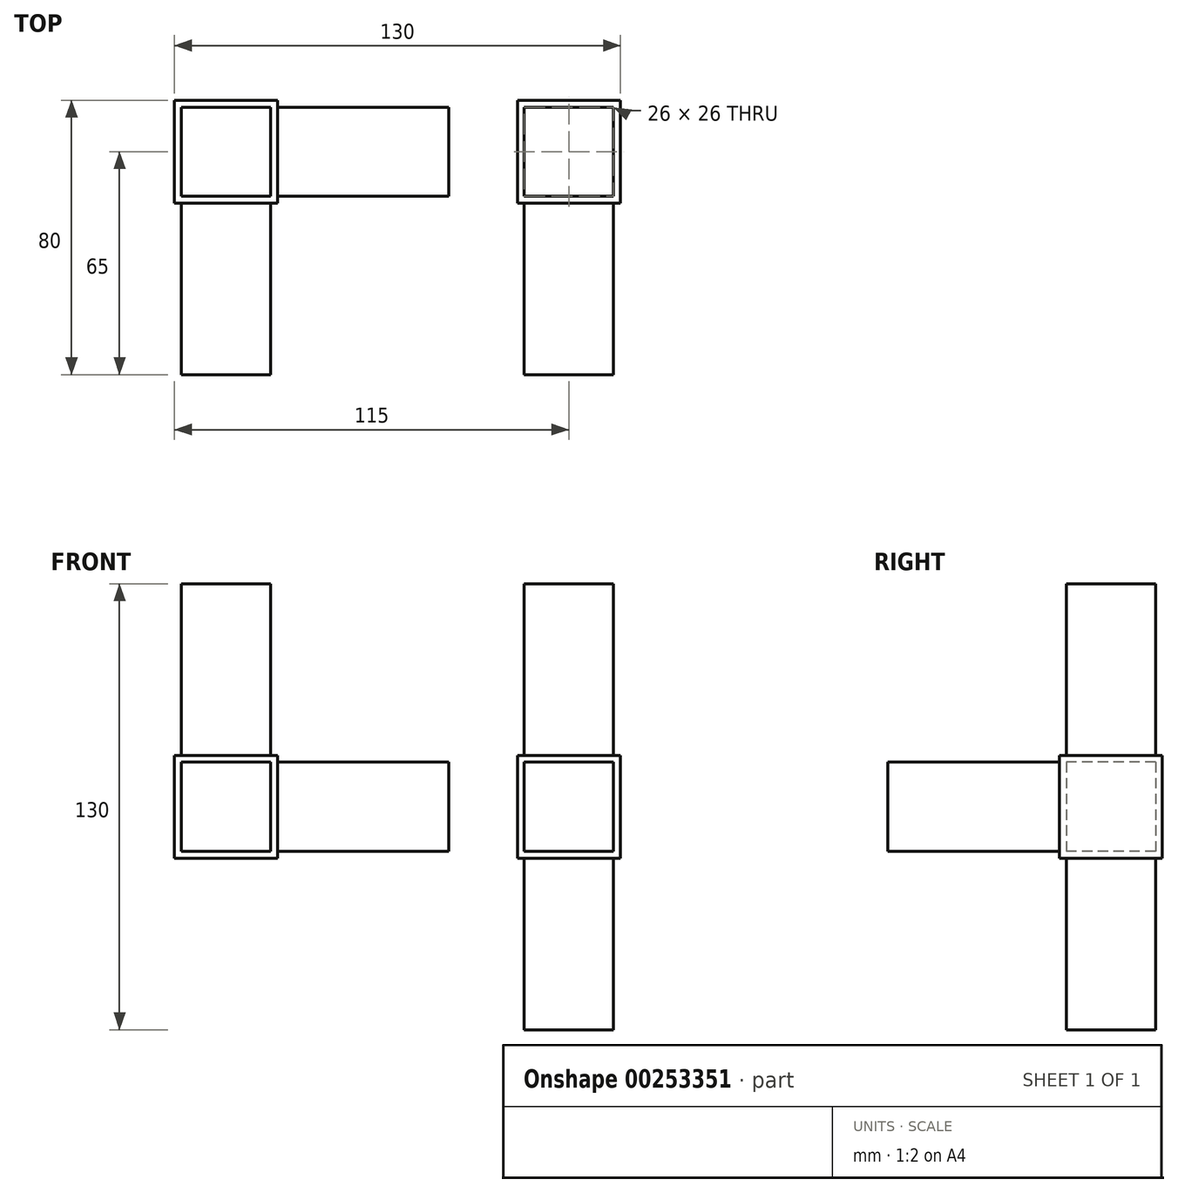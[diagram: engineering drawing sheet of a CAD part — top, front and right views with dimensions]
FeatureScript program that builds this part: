
annotation { "Feature Type Name" : "Feature", "Feature Type Description" : "" }
export const myFeature = defineFeature(function(context is Context, id is Id, definition is map)
    precondition{}
    {
        {
            assignVariable(context, id + "F0", {"name" : "Aussendurchmesser", "anyValue" : 30 * mm});
        }
        {
            assignVariable(context, id + "F1", {"name" : "Zapfenlaenge", "anyValue" : 50 * mm});
        }
        {
            var Q0;
            Q0=qCreatedBy(makeId("Top.planeOp"),FACE);
            var sketch = newSketch(context, id + "F2", { "sketchPlane" : qUnion([Q0])});
            skLineSegment(sketch, "E0.bottom", {"start": v(0, 0) * mm, "end": v(30, 0) * mm});
            skLineSegment(sketch, "E0.top", {"start": v(0, -30) * mm, "end": v(30, -30) * mm});
            skLineSegment(sketch, "E0.left", {"start": v(0, 0) * mm, "end": v(0, -30) * mm});
            skLineSegment(sketch, "E0.right", {"start": v(30, 0) * mm, "end": v(30, -30) * mm});
            skLineSegment(sketch, "E1.bottom", {"start": v(130, 0) * mm, "end": v(100, 0) * mm});
            skLineSegment(sketch, "E1.top", {"start": v(100, -30) * mm, "end": v(130, -30) * mm});
            skLineSegment(sketch, "E1.left", {"start": v(100, 0) * mm, "end": v(100, -30) * mm});
            skLineSegment(sketch, "E1.right", {"start": v(130, 0) * mm, "end": v(130, -30) * mm});
            skLineSegment(sketch, "E2.bottom", {"start": v(128, -2) * mm, "end": v(102, -2) * mm});
            skLineSegment(sketch, "E2.top", {"start": v(128, -28) * mm, "end": v(102, -28) * mm});
            skLineSegment(sketch, "E2.left", {"start": v(128, -2) * mm, "end": v(128, -28) * mm});
            skLineSegment(sketch, "E2.right", {"start": v(102, -2) * mm, "end": v(102, -28) * mm});
            skPoint(sketch, "E2.middle", {"position": v(115, -15) * mm});
            skLineSegment(sketch, "E3", {"start": v(100, -15) * mm, "end": v(115, -15) * mm, "construction": true});
            skLineSegment(sketch, "E4", {"start": v(115, -15) * mm, "end": v(115, 0) * mm, "construction": true});
            skSolve(sketch);
        }
        {
            var Q0;
            Q0=makeQuery(id+"F2.imprint","IMPRINT",FACE,{"disambiguationData":[TD([[makeQuery(id+"F2.imprint","IMPRINT",EDGE,{"derivedFrom":sQuery(id+"F2.wireOp",EDGE,"E0.bottom")}),-1.0]])]});
            extrude(context, id + "F3", {"entities" : qUnion([Q0]), "depth" : getVariable(context, 'Aussendurchmesser')});
        }
        {
            var Q0;
            Q0=makeQuery(id+"F3.opExtrude","SWEPT_FACE",FACE,{"disambiguationData":[OSD([sQuery(id+"F2.wireOp",EDGE,"E0.top")])]});
            var sketch = newSketch(context, id + "F4", { "sketchPlane" : qUnion([Q0])});
            skLineSegment(sketch, "E5.bottom", {"start": v(28, 28) * mm, "end": v(2, 28) * mm});
            skLineSegment(sketch, "E5.top", {"start": v(28, 2) * mm, "end": v(2, 2) * mm});
            skLineSegment(sketch, "E5.left", {"start": v(28, 28) * mm, "end": v(28, 2) * mm});
            skLineSegment(sketch, "E5.right", {"start": v(2, 28) * mm, "end": v(2, 2) * mm});
            skPoint(sketch, "E5.middle", {"position": v(15, 15) * mm});
            skLineSegment(sketch, "E6", {"start": v(15, 15) * mm, "end": v(15, 30) * mm, "construction": true});
            skLineSegment(sketch, "E7", {"start": v(15, 15) * mm, "end": v(0, 15) * mm, "construction": true});
            skSolve(sketch);
        }
        {
            var Q0;
            Q0 = qSketchRegion(id + "F4", true);
            extrude(context, id + "F5", {"entities" : qUnion([Q0]), "operationType" : NewBodyOperationType.ADD, "depth" : getVariable(context, 'Zapfenlaenge')});
        }
        {
            var Q0;
            Q0=makeQuery(id+"F3.opExtrude","SWEPT_FACE",FACE,{"disambiguationData":[OSD([sQuery(id+"F2.wireOp",EDGE,"E0.right")])]});
            var sketch = newSketch(context, id + "F6", { "sketchPlane" : qUnion([Q0])});
            skLineSegment(sketch, "E8.bottom", {"start": v(-2, 28) * mm, "end": v(-28, 28) * mm});
            skLineSegment(sketch, "E8.top", {"start": v(-2, 2) * mm, "end": v(-28, 2) * mm});
            skLineSegment(sketch, "E8.left", {"start": v(-2, 28) * mm, "end": v(-2, 2) * mm});
            skLineSegment(sketch, "E8.right", {"start": v(-28, 28) * mm, "end": v(-28, 2) * mm});
            skPoint(sketch, "E8.middle", {"position": v(-15, 15) * mm});
            skLineSegment(sketch, "E9", {"start": v(-15, 15) * mm, "end": v(0, 15) * mm, "construction": true});
            skLineSegment(sketch, "E10", {"start": v(-15, 15) * mm, "end": v(-15, 30) * mm, "construction": true});
            skSolve(sketch);
        }
        {
            var Q0;
            Q0 = qSketchRegion(id + "F6", true);
            extrude(context, id + "F7", {"entities" : qUnion([Q0]), "operationType" : NewBodyOperationType.ADD, "depth" : getVariable(context, 'Zapfenlaenge')});
        }
        {
            var Q0;
            Q0=makeQuery(id+"F3.opExtrude","CAP_FACE",FACE,{"disambiguationData":[OSD([sQuery(id+"F2.wireOp",EDGE,"E0.bottom"),sQuery(id+"F2.wireOp",EDGE,"E0.top"),sQuery(id+"F2.wireOp",EDGE,"E0.left"),sQuery(id+"F2.wireOp",EDGE,"E0.right")])],"isStart":false});
            var sketch = newSketch(context, id + "F8", { "sketchPlane" : qUnion([Q0])});
            skLineSegment(sketch, "E11.bottom", {"start": v(28, -28) * mm, "end": v(2, -28) * mm});
            skLineSegment(sketch, "E11.top", {"start": v(28, -2) * mm, "end": v(2, -2) * mm});
            skLineSegment(sketch, "E11.left", {"start": v(28, -28) * mm, "end": v(28, -2) * mm});
            skLineSegment(sketch, "E11.right", {"start": v(2, -28) * mm, "end": v(2, -2) * mm});
            skPoint(sketch, "E11.middle", {"position": v(15, -15) * mm});
            skLineSegment(sketch, "E12", {"start": v(15, -15) * mm, "end": v(30, -15) * mm, "construction": true});
            skLineSegment(sketch, "E13", {"start": v(15, -15) * mm, "end": v(15, -30) * mm, "construction": true});
            skSolve(sketch);
        }
        {
            var Q0;
            Q0 = qSketchRegion(id + "F8", true);
            extrude(context, id + "F9", {"entities" : qUnion([Q0]), "operationType" : NewBodyOperationType.ADD, "depth" : getVariable(context, 'Zapfenlaenge')});
        }
        {
            var Q0;
            Q0=makeQuery(id+"F2.imprint","IMPRINT",FACE,{"disambiguationData":[TD([[makeQuery(id+"F2.imprint","IMPRINT",EDGE,{"derivedFrom":sQuery(id+"F2.wireOp",EDGE,"E1.bottom")}),-1.0]])]});
            var Q1;
            Q1=makeQuery(id+"F2.imprint","IMPRINT",FACE,{"disambiguationData":[TD([[makeQuery(id+"F2.imprint","IMPRINT",EDGE,{"derivedFrom":sQuery(id+"F2.wireOp",EDGE,"E2.bottom")}),1.0]])]});
            var Q2;
            Q2=makeQuery(id+"F2.imprint","IMPRINT",FACE,{"disambiguationData":[TD([[makeQuery(id+"F2.imprint","IMPRINT",EDGE,{"derivedFrom":sQuery(id+"F2.wireOp",EDGE,"E1.bottom")}),1.0]])]});
            extrude(context, id + "F10", {"entities" : qUnion([Q0, Q1, Q2]), "depth" : getVariable(context, 'Aussendurchmesser')});
        }
        {
            var Q0;
            Q0=makeQuery(id+"F10.opExtrude","CAP_FACE",FACE,{"disambiguationData":[OSD([sQuery(id+"F2.wireOp",EDGE,"E1.bottom"),sQuery(id+"F2.wireOp",EDGE,"E1.top"),sQuery(id+"F2.wireOp",EDGE,"E1.left"),sQuery(id+"F2.wireOp",EDGE,"E1.right")])],"isStart":false});
            var sketch = newSketch(context, id + "F11", { "sketchPlane" : qUnion([Q0])});
            skLineSegment(sketch, "E14.bottom", {"start": v(102, -2) * mm, "end": v(128, -2) * mm});
            skLineSegment(sketch, "E14.top", {"start": v(102, -28) * mm, "end": v(128, -28) * mm});
            skLineSegment(sketch, "E14.left", {"start": v(102, -2) * mm, "end": v(102, -28) * mm});
            skLineSegment(sketch, "E14.right", {"start": v(128, -2) * mm, "end": v(128, -28) * mm});
            skPoint(sketch, "E14.middle", {"position": v(115, -15) * mm});
            skLineSegment(sketch, "E15", {"start": v(115, -15) * mm, "end": v(100, -15) * mm, "construction": true});
            skLineSegment(sketch, "E16", {"start": v(115, -15) * mm, "end": v(115, 0) * mm, "construction": true});
            skSolve(sketch);
        }
        {
            var Q0;
            Q0=makeQuery(id+"F11.imprint","IMPRINT",FACE,{"disambiguationData":[TD([[makeQuery(id+"F11.imprint","IMPRINT",EDGE,{"derivedFrom":sQuery(id+"F11.wireOp",EDGE,"E14.bottom")}),-1.0]])]});
            extrude(context, id + "F12", {"entities" : qUnion([Q0]), "operationType" : NewBodyOperationType.ADD, "depth" : getVariable(context, 'Zapfenlaenge')});
        }
        {
            var Q0;
            Q0=makeQuery(id+"F10.opExtrude","SWEPT_FACE",FACE,{"disambiguationData":[OSD([sQuery(id+"F2.wireOp",EDGE,"E1.top")])]});
            var sketch = newSketch(context, id + "F13", { "sketchPlane" : qUnion([Q0])});
            skLineSegment(sketch, "E17.bottom", {"start": v(102, 28) * mm, "end": v(128, 28) * mm});
            skLineSegment(sketch, "E17.top", {"start": v(102, 2) * mm, "end": v(128, 2) * mm});
            skLineSegment(sketch, "E17.left", {"start": v(102, 28) * mm, "end": v(102, 2) * mm});
            skLineSegment(sketch, "E17.right", {"start": v(128, 28) * mm, "end": v(128, 2) * mm});
            skPoint(sketch, "E17.middle", {"position": v(115, 15) * mm});
            skLineSegment(sketch, "E18", {"start": v(115, 15) * mm, "end": v(115, 30) * mm, "construction": true});
            skLineSegment(sketch, "E19", {"start": v(115, 15) * mm, "end": v(100, 15) * mm, "construction": true});
            skSolve(sketch);
        }
        {
            var Q0;
            Q0=makeQuery(id+"F13.imprint","IMPRINT",FACE,{"disambiguationData":[TD([[makeQuery(id+"F13.imprint","IMPRINT",EDGE,{"derivedFrom":sQuery(id+"F13.wireOp",EDGE,"E17.bottom")}),-1.0]])]});
            extrude(context, id + "F14", {"entities" : qUnion([Q0]), "operationType" : NewBodyOperationType.ADD, "depth" : getVariable(context, 'Zapfenlaenge')});
        }
        {
            var Q0;
            Q0=makeQuery(id+"F2.imprint","IMPRINT",FACE,{"disambiguationData":[TD([[makeQuery(id+"F2.imprint","IMPRINT",EDGE,{"derivedFrom":sQuery(id+"F2.wireOp",EDGE,"E2.bottom")}),1.0]])]});
            extrude(context, id + "F15", {"entities" : qUnion([Q0]), "operationType" : NewBodyOperationType.ADD, "oppositeDirection" : true, "depth" : getVariable(context, 'Zapfenlaenge')});
        }
    });
